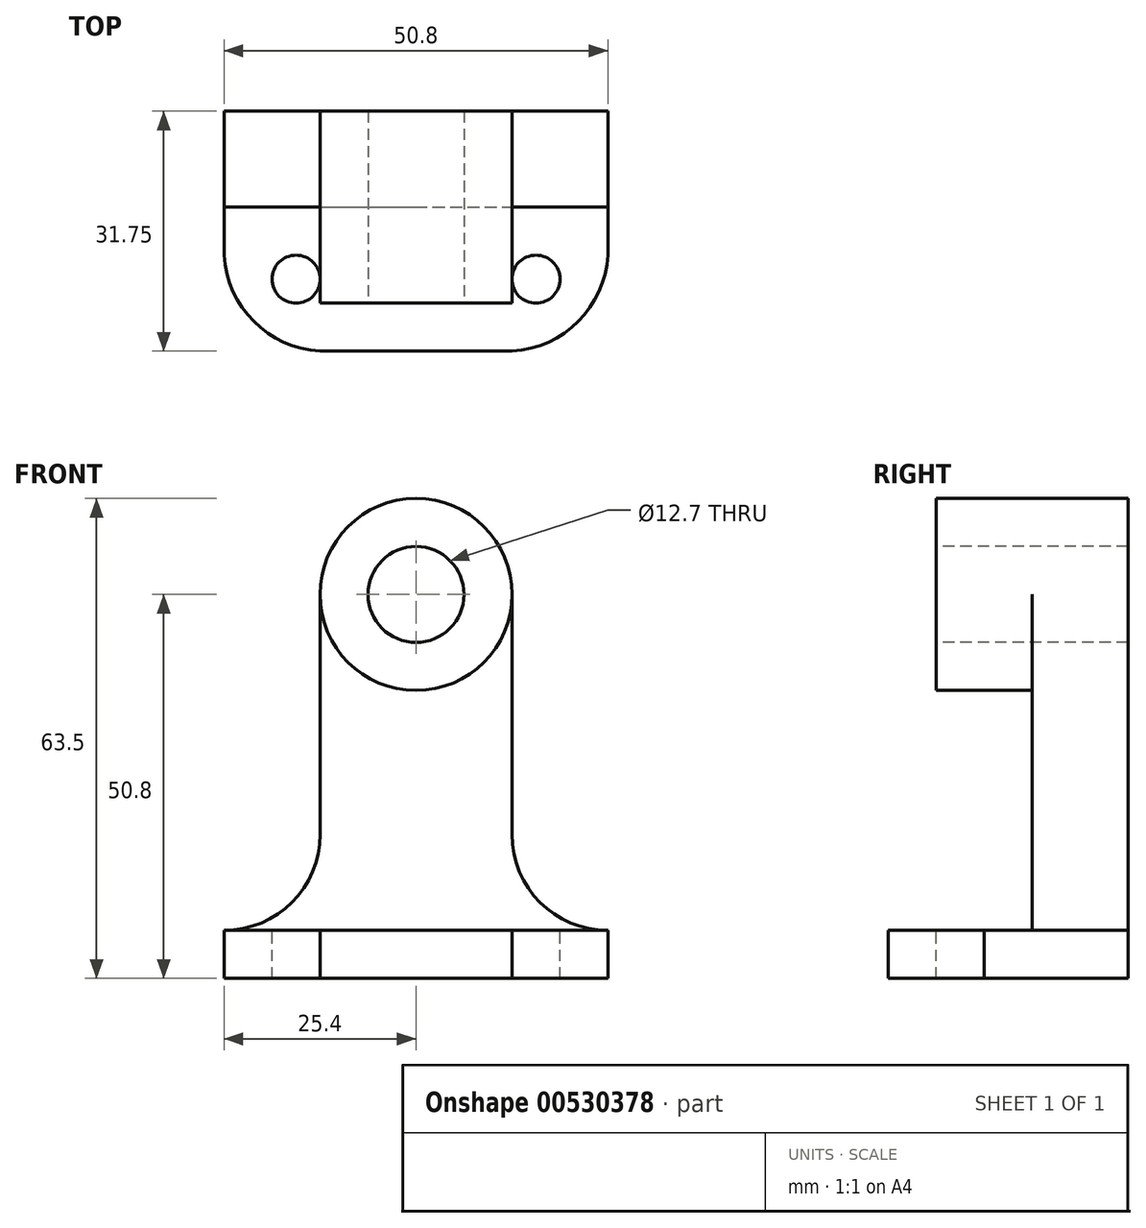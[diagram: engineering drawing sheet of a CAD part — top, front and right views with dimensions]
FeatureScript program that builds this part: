
annotation { "Feature Type Name" : "Feature", "Feature Type Description" : "" }
export const myFeature = defineFeature(function(context is Context, id is Id, definition is map)
    precondition{}
    {
        {
            var Q0;
            Q0=qCreatedBy(makeId("Top.planeOp"),FACE);
            var sketch = newSketch(context, id + "F0", { "sketchPlane" : qUnion([Q0])});
            skLineSegment(sketch, "E0", {"start": v(-50.8, 31.75) * mm, "end": v(-50.8, 12.7) * mm});
            skLineSegment(sketch, "E1", {"start": v(-38.1, 0) * mm, "end": v(-12.7, 0) * mm});
            skLineSegment(sketch, "E2", {"start": v(0, 12.7) * mm, "end": v(0, 31.75) * mm});
            skLineSegment(sketch, "E3", {"start": v(0, 31.75) * mm, "end": v(-50.8, 31.75) * mm});
            skArc(sketch, "E4", {"start": v(-50.8, 12.7) * mm, "mid": v(-46.87, 3.93) * mm, "end": v(-38.1, 0) * mm});
            skArc(sketch, "E5", {"start": v(-12.7, 0) * mm, "mid": v(-3.93, 3.93) * mm, "end": v(0, 12.7) * mm});
            skPoint(sketch, "E6.orphan", {"position": v(-50.8, 0) * mm});
            skPoint(sketch, "E7.orphan", {"position": v(0, 0) * mm});
            skSolve(sketch);
        }
        {
            var Q0;
            Q0=makeQuery(id+"F0.imprint","IMPRINT",FACE,{"disambiguationData":[TD([[makeQuery(id+"F0.imprint","IMPRINT",EDGE,{"derivedFrom":sQuery(id+"F0.wireOp",EDGE,"E0")}),1.0]])]});
            extrude(context, id + "F1", {"entities" : qUnion([Q0]), "depth" : 6.35 * mm, "offsetDistance" : 25.4 * mm});
        }
        {
            var Q0;
            Q0=makeQuery(id+"F1.opExtrude","CAP_FACE",FACE,{"disambiguationData":[OSD([sQuery(id+"F0.wireOp",EDGE,"E0"),sQuery(id+"F0.wireOp",EDGE,"E1"),sQuery(id+"F0.wireOp",EDGE,"E2"),sQuery(id+"F0.wireOp",EDGE,"E3"),sQuery(id+"F0.wireOp",EDGE,"E4"),sQuery(id+"F0.wireOp",EDGE,"E5")])],"isStart":false});
            var sketch = newSketch(context, id + "F2", { "sketchPlane" : qUnion([Q0])});
            skLineSegment(sketch, "E8", {"start": v(-38.1, 31.75) * mm, "end": v(-38.1, 19.05) * mm});
            skLineSegment(sketch, "E9", {"start": v(-38.1, 19.05) * mm, "end": v(-12.7, 19.05) * mm});
            skLineSegment(sketch, "E10", {"start": v(-12.7, 19.05) * mm, "end": v(-12.7, 31.75) * mm});
            skLineSegment(sketch, "E11", {"start": v(-12.7, 31.75) * mm, "end": v(-38.1, 31.75) * mm});
            skSolve(sketch);
        }
        {
            var Q0;
            Q0=makeQuery(id+"F2.imprint","IMPRINT",FACE,{"disambiguationData":[TD([[makeQuery(id+"F2.imprint","IMPRINT",EDGE,{"derivedFrom":sQuery(id+"F2.wireOp",EDGE,"E8")}),1.0]])]});
            extrude(context, id + "F3", {"entities" : qUnion([Q0]), "operationType" : NewBodyOperationType.ADD, "depth" : 57.15 * mm, "offsetDistance" : 25.4 * mm});
        }
        {
            var Q0;
            Q0=makeQuery(id+"F3.opExtrude","SWEPT_FACE",FACE,{"disambiguationData":[OSD([sQuery(id+"F2.wireOp",EDGE,"E9")])]});
            var sketch = newSketch(context, id + "F4", { "sketchPlane" : qUnion([Q0])});
            skCircle(sketch, "E12", {"center": v(-25.4, 50.8) * mm, "radius": 12.7 * mm});
            skSolve(sketch);
        }
        {
            var Q0;
            {var subQ0=sQuery(id+"F4.wireOp",EDGE,"E12");var subQ1=sQuery(id+"F2.wireOp",EDGE,"E9");var subQ2=makeQuery(id+"F3.opExtrude","CAP_EDGE",EDGE,{"disambiguationData":[OSD([subQ1])],"isStart":false});var subQ3=makeQuery(id+"F4.imprint","INTERSECT",VERTEX,{"derivedFrom":[subQ2,subQ0]});Q0=makeQuery(id+"F4.imprint","IMPRINT",FACE,{"disambiguationData":[TD([[makeQuery(id+"F4.imprint","IMPRINT",EDGE,{"disambiguationData":[TD([[subQ3,-1.0]])],"derivedFrom":subQ0}),-1.0]])]});}
            var Q1;
            {var subQ0=sQuery(id+"F4.wireOp",EDGE,"E12");var subQ1=sQuery(id+"F2.wireOp",EDGE,"E9");var subQ2=makeQuery(id+"F3.opExtrude","CAP_EDGE",EDGE,{"disambiguationData":[OSD([subQ1])],"isStart":false});var subQ3=makeQuery(id+"F4.imprint","INTERSECT",VERTEX,{"derivedFrom":[subQ2,subQ0]});Q1=makeQuery(id+"F4.imprint","IMPRINT",FACE,{"disambiguationData":[TD([[makeQuery(id+"F4.imprint","IMPRINT",EDGE,{"disambiguationData":[TD([[subQ3,1.0]])],"derivedFrom":subQ0}),-1.0]])]});}
            extrude(context, id + "F5", {"entities" : qUnion([Q0, Q1]), "operationType" : NewBodyOperationType.REMOVE, "endBound" : BoundingType.THROUGH_ALL, "oppositeDirection" : true, "depth" : 25.4 * mm, "offsetDistance" : 25.4 * mm});
        }
        {
            var Q0;
            {var subQ0=sQuery(id+"F4.wireOp",EDGE,"E12");var subQ1=sQuery(id+"F2.wireOp",EDGE,"E9");var subQ2=makeQuery(id+"F4.imprint","INTERSECT",VERTEX,{"derivedFrom":[makeQuery(id+"F3.opExtrude","CAP_EDGE",EDGE,{"disambiguationData":[OSD([subQ1])],"isStart":false}),subQ0]});Q0=makeQuery(id+"F4.imprint","IMPRINT",FACE,{"disambiguationData":[TD([[makeQuery(id+"F4.imprint","IMPRINT",EDGE,{"disambiguationData":[TD([[subQ2,1.0]])],"derivedFrom":subQ0}),1.0]])]});}
            extrude(context, id + "F6", {"entities" : qUnion([Q0]), "operationType" : NewBodyOperationType.ADD, "depth" : 12.7 * mm, "offsetDistance" : 25.4 * mm});
        }
        {
            var Q0;
            Q0=makeQuery(id+"F6.opExtrude","CAP_FACE",FACE,{"disambiguationData":[OSD([sQuery(id+"F4.wireOp",EDGE,"E12")])],"isStart":false});
            var sketch = newSketch(context, id + "F7", { "sketchPlane" : qUnion([Q0])});
            skCircle(sketch, "E13", {"center": v(-25.4, 50.8) * mm, "radius": 6.35 * mm});
            skSolve(sketch);
        }
        {
            var Q0;
            Q0=makeQuery(id+"F7.imprint","IMPRINT",FACE,{"disambiguationData":[TD([[makeQuery(id+"F7.imprint","IMPRINT",EDGE,{"derivedFrom":sQuery(id+"F7.wireOp",EDGE,"E13")}),1.0]])]});
            extrude(context, id + "F8", {"entities" : qUnion([Q0]), "operationType" : NewBodyOperationType.REMOVE, "endBound" : BoundingType.THROUGH_ALL, "oppositeDirection" : true, "depth" : 25.4 * mm, "offsetDistance" : 25.4 * mm});
        }
        {
            var Q0;
            Q0=makeQuery(id+"F1.opExtrude","CAP_FACE",FACE,{"disambiguationData":[OSD([sQuery(id+"F0.wireOp",EDGE,"E0"),sQuery(id+"F0.wireOp",EDGE,"E1"),sQuery(id+"F0.wireOp",EDGE,"E2"),sQuery(id+"F0.wireOp",EDGE,"E3"),sQuery(id+"F0.wireOp",EDGE,"E4"),sQuery(id+"F0.wireOp",EDGE,"E5")])],"isStart":false});
            var sketch = newSketch(context, id + "F9", { "sketchPlane" : qUnion([Q0])});
            skLineSegment(sketch, "E14", {"start": v(0, 31.75) * mm, "end": v(-12.7, 31.75) * mm});
            skLineSegment(sketch, "E15", {"start": v(-50.8, 19.05) * mm, "end": v(-38.06, 19.05) * mm});
            skLineSegment(sketch, "E16", {"start": v(-38.06, 19.05) * mm, "end": v(-38.1, 31.75) * mm});
            skLineSegment(sketch, "E17", {"start": v(-38.1, 31.75) * mm, "end": v(-50.8, 31.75) * mm});
            skLineSegment(sketch, "E18", {"start": v(-50.8, 31.75) * mm, "end": v(-50.8, 19.05) * mm});
            skLineSegment(sketch, "E19", {"start": v(-12.7, 31.75) * mm, "end": v(-12.7, 19.05) * mm});
            skLineSegment(sketch, "E20", {"start": v(-12.7, 19.05) * mm, "end": v(0, 19.05) * mm});
            skLineSegment(sketch, "E21", {"start": v(0, 19.05) * mm, "end": v(0, 31.75) * mm});
            skSolve(sketch);
        }
        {
            var Q0;
            Q0=makeQuery(id+"F9.imprint","IMPRINT",FACE,{"disambiguationData":[TD([[makeQuery(id+"F9.imprint","IMPRINT",EDGE,{"derivedFrom":sQuery(id+"F9.wireOp",EDGE,"E17")}),1.0]])]});
            var Q1;
            Q1=makeQuery(id+"F9.imprint","IMPRINT",FACE,{"disambiguationData":[TD([[makeQuery(id+"F9.imprint","IMPRINT",EDGE,{"derivedFrom":sQuery(id+"F9.wireOp",EDGE,"E14")}),1.0]])]});
            extrude(context, id + "F10", {"entities" : qUnion([Q0, Q1]), "operationType" : NewBodyOperationType.ADD, "depth" : 25.4 * mm, "offsetDistance" : 25.4 * mm});
        }
        {
            var Q0;
            Q0=makeQuery(id+"F10.boolean.opBoolean","MERGE",FACE,{"derivedFrom":[makeQuery(id+"F3.opExtrude","SWEPT_FACE",FACE,{"disambiguationData":[OSD([sQuery(id+"F2.wireOp",EDGE,"E9")])]}),makeQuery(id+"F10.opExtrude","SWEPT_FACE",FACE,{"disambiguationData":[OSD([sQuery(id+"F9.wireOp",EDGE,"E15")])]}),makeQuery(id+"F10.opExtrude","SWEPT_FACE",FACE,{"disambiguationData":[OSD([sQuery(id+"F9.wireOp",EDGE,"E20")])]})]});
            var sketch = newSketch(context, id + "F11", { "sketchPlane" : qUnion([Q0])});
            skLineSegment(sketch, "E22", {"start": v(-38.1, 31.75) * mm, "end": v(-38.1, 6.35) * mm});
            skLineSegment(sketch, "E23", {"start": v(-38.1, 6.35) * mm, "end": v(-50.8, 6.35) * mm});
            skArc(sketch, "E24", {"start": v(-50.8, 6.35) * mm, "mid": v(-41.82, 10.07) * mm, "end": v(-38.1, 19.05) * mm});
            skLineSegment(sketch, "E25", {"start": v(-12.7, 31.75) * mm, "end": v(-12.7, 6.35) * mm});
            skLineSegment(sketch, "E26", {"start": v(-12.7, 6.35) * mm, "end": v(0, 6.35) * mm});
            skArc(sketch, "E27", {"start": v(-12.7, 19.05) * mm, "mid": v(-8.98, 10.07) * mm, "end": v(0, 6.35) * mm});
            skLineSegment(sketch, "E28", {"start": v(-50.8, 6.35) * mm, "end": v(-50.8, 31.75) * mm});
            skLineSegment(sketch, "E29", {"start": v(-50.8, 31.75) * mm, "end": v(-38.1, 31.75) * mm});
            skLineSegment(sketch, "E30", {"start": v(-12.7, 31.75) * mm, "end": v(0, 31.75) * mm});
            skLineSegment(sketch, "E31", {"start": v(0, 31.75) * mm, "end": v(0, 6.35) * mm});
            skSolve(sketch);
        }
        {
            var Q0;
            {var subQ2=sQuery(id+"F11.wireOp",EDGE,"E24");Q0=makeQuery(id+"F11.imprint","IMPRINT",FACE,{"disambiguationData":[TD([[makeQuery(id+"F11.imprint","IMPRINT",EDGE,{"derivedFrom":subQ2}),1.0]])]});}
            var Q1;
            {var subQ2=sQuery(id+"F11.wireOp",EDGE,"E27");Q1=makeQuery(id+"F11.imprint","IMPRINT",FACE,{"disambiguationData":[TD([[makeQuery(id+"F11.imprint","IMPRINT",EDGE,{"derivedFrom":subQ2}),1.0]])]});}
            extrude(context, id + "F12", {"entities" : qUnion([Q0, Q1]), "operationType" : NewBodyOperationType.REMOVE, "endBound" : BoundingType.THROUGH_ALL, "oppositeDirection" : true, "depth" : 25.4 * mm, "offsetDistance" : 25.4 * mm});
        }
        {
            var Q0;
            Q0=makeQuery(id+"F1.opExtrude","CAP_FACE",FACE,{"disambiguationData":[OSD([sQuery(id+"F0.wireOp",EDGE,"E0"),sQuery(id+"F0.wireOp",EDGE,"E1"),sQuery(id+"F0.wireOp",EDGE,"E2"),sQuery(id+"F0.wireOp",EDGE,"E3"),sQuery(id+"F0.wireOp",EDGE,"E4"),sQuery(id+"F0.wireOp",EDGE,"E5")])],"isStart":false});
            var sketch = newSketch(context, id + "F13", { "sketchPlane" : qUnion([Q0])});
            skCircle(sketch, "E32", {"center": v(-9.53, 9.53) * mm, "radius": 3.18 * mm});
            skCircle(sketch, "E33", {"center": v(-41.27, 9.53) * mm, "radius": 3.18 * mm});
            skSolve(sketch);
        }
        {
            var Q0;
            Q0=makeQuery(id+"F13.imprint","IMPRINT",FACE,{"disambiguationData":[TD([[makeQuery(id+"F13.imprint","IMPRINT",EDGE,{"derivedFrom":sQuery(id+"F13.wireOp",EDGE,"E33")}),1.0]])]});
            var Q1;
            Q1=makeQuery(id+"F13.imprint","IMPRINT",FACE,{"disambiguationData":[TD([[makeQuery(id+"F13.imprint","IMPRINT",EDGE,{"derivedFrom":sQuery(id+"F13.wireOp",EDGE,"E32")}),1.0]])]});
            extrude(context, id + "F14", {"entities" : qUnion([Q0, Q1]), "operationType" : NewBodyOperationType.REMOVE, "endBound" : BoundingType.THROUGH_ALL, "oppositeDirection" : true, "depth" : 25.4 * mm, "offsetDistance" : 25.4 * mm});
        }
    });
